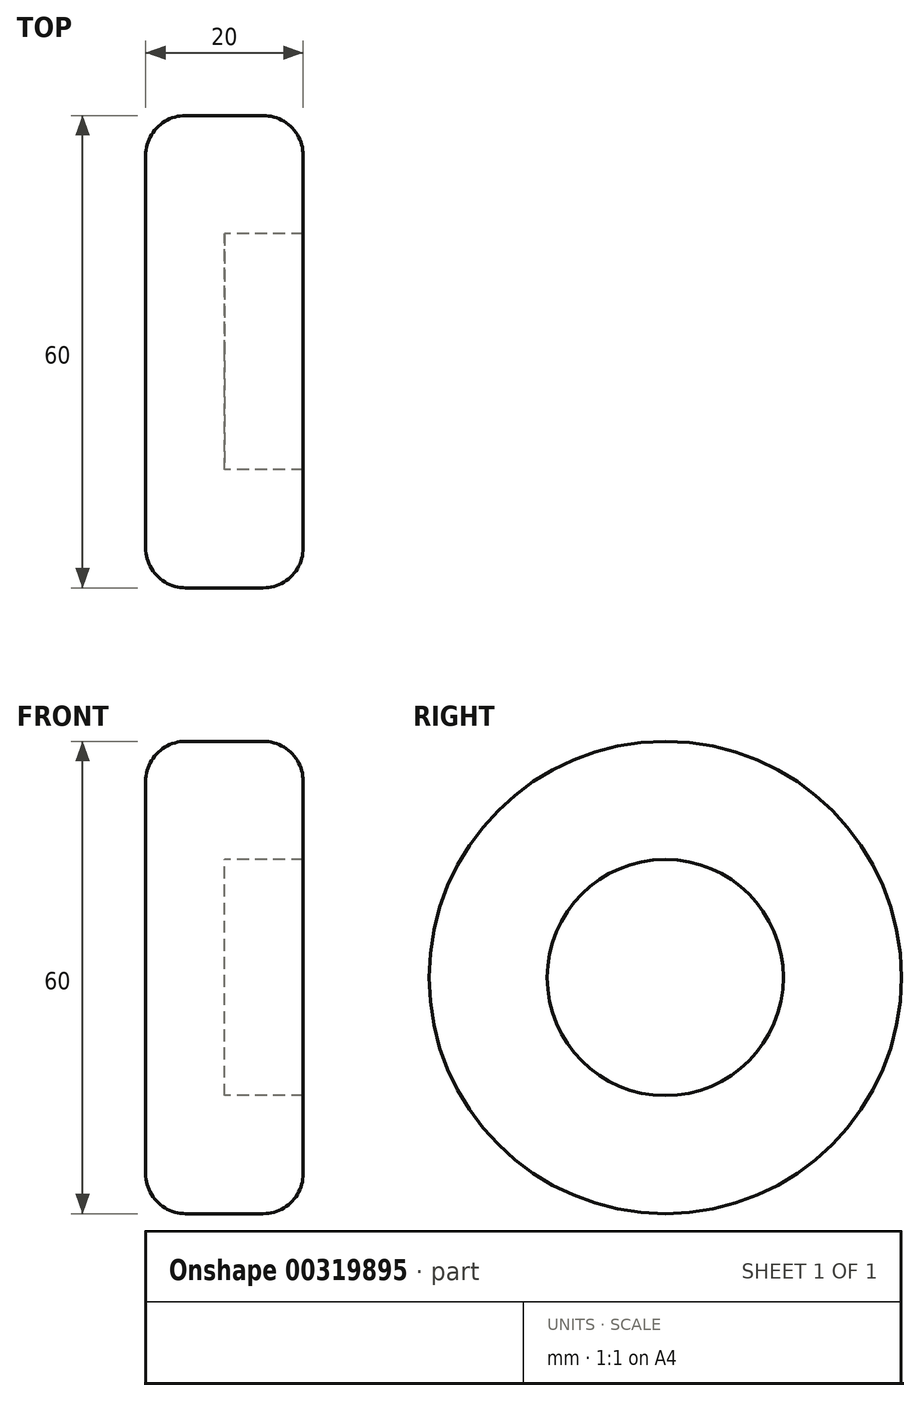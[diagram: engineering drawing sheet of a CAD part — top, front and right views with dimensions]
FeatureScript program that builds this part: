
annotation { "Feature Type Name" : "Feature", "Feature Type Description" : "" }
export const myFeature = defineFeature(function(context is Context, id is Id, definition is map)
    precondition{}
    {
        {
            var Q0;
            Q0=qCreatedBy(makeId("Right.planeOp"),FACE);
            var sketch = newSketch(context, id + "F0", { "sketchPlane" : qUnion([Q0])});
            skCircle(sketch, "E0", {"center": v(0, 0) * mm, "radius": 15 * mm});
            skCircle(sketch, "E1", {"center": v(0, 0) * mm, "radius": 30 * mm});
            skLineSegment(sketch, "E2", {"start": v(0, 0) * mm, "end": v(15, 0) * mm});
            skLineSegment(sketch, "E3", {"start": v(0, 0) * mm, "end": v(-30, 0) * mm});
            skSolve(sketch);
        }
        {
            var Q0;
            Q0=makeQuery(id+"F0.imprint","IMPRINT",FACE,{"disambiguationData":[TD([[makeQuery(id+"F0.imprint","IMPRINT",EDGE,{"derivedFrom":sQuery(id+"F0.wireOp",EDGE,"E1")}),1.0]])]});
            extrude(context, id + "F1", {"entities" : qUnion([Q0]), "depth" : 20 * mm});
        }
        {
            var Q0;
            {var subQ0=sQuery(id+"F0.wireOp",EDGE,"E2");Q0=makeQuery(id+"F0.imprint","IMPRINT",FACE,{"disambiguationData":[TD([[makeQuery(id+"F0.imprint","IMPRINT",EDGE,{"derivedFrom":subQ0}),1.0]])]});}
            var Q1;
            {var subQ0=sQuery(id+"F0.wireOp",EDGE,"E2");Q1=makeQuery(id+"F0.imprint","IMPRINT",FACE,{"disambiguationData":[TD([[makeQuery(id+"F0.imprint","IMPRINT",EDGE,{"derivedFrom":subQ0}),-1.0]])]});}
            extrude(context, id + "F2", {"entities" : qUnion([Q0, Q1]), "operationType" : NewBodyOperationType.ADD, "depth" : 10 * mm});
        }
        {
            var Q0;
            Q0=makeQuery(id+"F1.opExtrude","SWEPT_BODY",BODY,{"disambiguationData":[OSD([sQuery(id+"F0.wireOp",EDGE,"E0"),sQuery(id+"F0.wireOp",EDGE,"E1")])]});
            transform(context, id + "F3", {"entities" : qUnion([Q0]), "transformType" : TransformType.TRANSLATION_3D, "dx" : 0 * mm, "dy" : 0 * mm, "dz" : 83.82 * mm, "makeCopy" : true});
        }
        {
            var Q0;
            Q0=makeQuery(id+"F3.opPattern","COPY",BODY,{"derivedFrom":makeQuery(id+"F1.opExtrude","SWEPT_BODY",BODY,{"disambiguationData":[OSD([sQuery(id+"F0.wireOp",EDGE,"E0"),sQuery(id+"F0.wireOp",EDGE,"E1")])]}),"instanceName":"1"});
            transform(context, id + "F4", {"entities" : qUnion([Q0]), "transformType" : TransformType.TRANSLATION_3D, "dx" : 0 * mm, "dy" : -105.66 * mm, "dz" : 0 * mm, "makeCopy" : true});
        }
        {
            var Q0;
            Q0=makeQuery(id+"F4.opPattern","COPY",BODY,{"derivedFrom":makeQuery(id+"F3.opPattern","COPY",BODY,{"derivedFrom":makeQuery(id+"F1.opExtrude","SWEPT_BODY",BODY,{"disambiguationData":[OSD([sQuery(id+"F0.wireOp",EDGE,"E0"),sQuery(id+"F0.wireOp",EDGE,"E1")])]}),"instanceName":"1"}),"instanceName":"1"});
            transform(context, id + "F5", {"entities" : qUnion([Q0]), "transformType" : TransformType.TRANSLATION_3D, "dx" : 0 * mm, "dy" : 0 * mm, "dz" : -88.65 * mm, "makeCopy" : true});
        }
        {
            var Q0;
            Q0=makeQuery(id+"F3.opPattern","COPY",BODY,{"derivedFrom":makeQuery(id+"F1.opExtrude","SWEPT_BODY",BODY,{"disambiguationData":[OSD([sQuery(id+"F0.wireOp",EDGE,"E0"),sQuery(id+"F0.wireOp",EDGE,"E1")])]}),"instanceName":"1"});
            var Q1;
            Q1=makeQuery(id+"F4.opPattern","COPY",BODY,{"derivedFrom":makeQuery(id+"F3.opPattern","COPY",BODY,{"derivedFrom":makeQuery(id+"F1.opExtrude","SWEPT_BODY",BODY,{"disambiguationData":[OSD([sQuery(id+"F0.wireOp",EDGE,"E0"),sQuery(id+"F0.wireOp",EDGE,"E1")])]}),"instanceName":"1"}),"instanceName":"1"});
            var Q2;
            Q2=makeQuery(id+"F5.opPattern","COPY",BODY,{"derivedFrom":makeQuery(id+"F4.opPattern","COPY",BODY,{"derivedFrom":makeQuery(id+"F3.opPattern","COPY",BODY,{"derivedFrom":makeQuery(id+"F1.opExtrude","SWEPT_BODY",BODY,{"disambiguationData":[OSD([sQuery(id+"F0.wireOp",EDGE,"E0"),sQuery(id+"F0.wireOp",EDGE,"E1")])]}),"instanceName":"1"}),"instanceName":"1"}),"instanceName":"1"});
            deleteBodies(context, id + "F6", {"entities" : qUnion([Q0, Q1, Q2])});
        }
        {
            var Q0;
            Q0=makeQuery(id+"F1.opExtrude","CAP_EDGE",EDGE,{"disambiguationData":[OSD([sQuery(id+"F0.wireOp",EDGE,"E1")])],"isStart":true});
            var Q1;
            Q1=makeQuery(id+"F1.opExtrude","CAP_EDGE",EDGE,{"disambiguationData":[OSD([sQuery(id+"F0.wireOp",EDGE,"E1")])],"isStart":false});
            fillet(context, id + "F7", {"entities" : qUnion([Q0, Q1]), "radius" : 5.08 * mm, "tangentPropagation" : true, "allowEdgeOverflow" : false});
        }
    });
